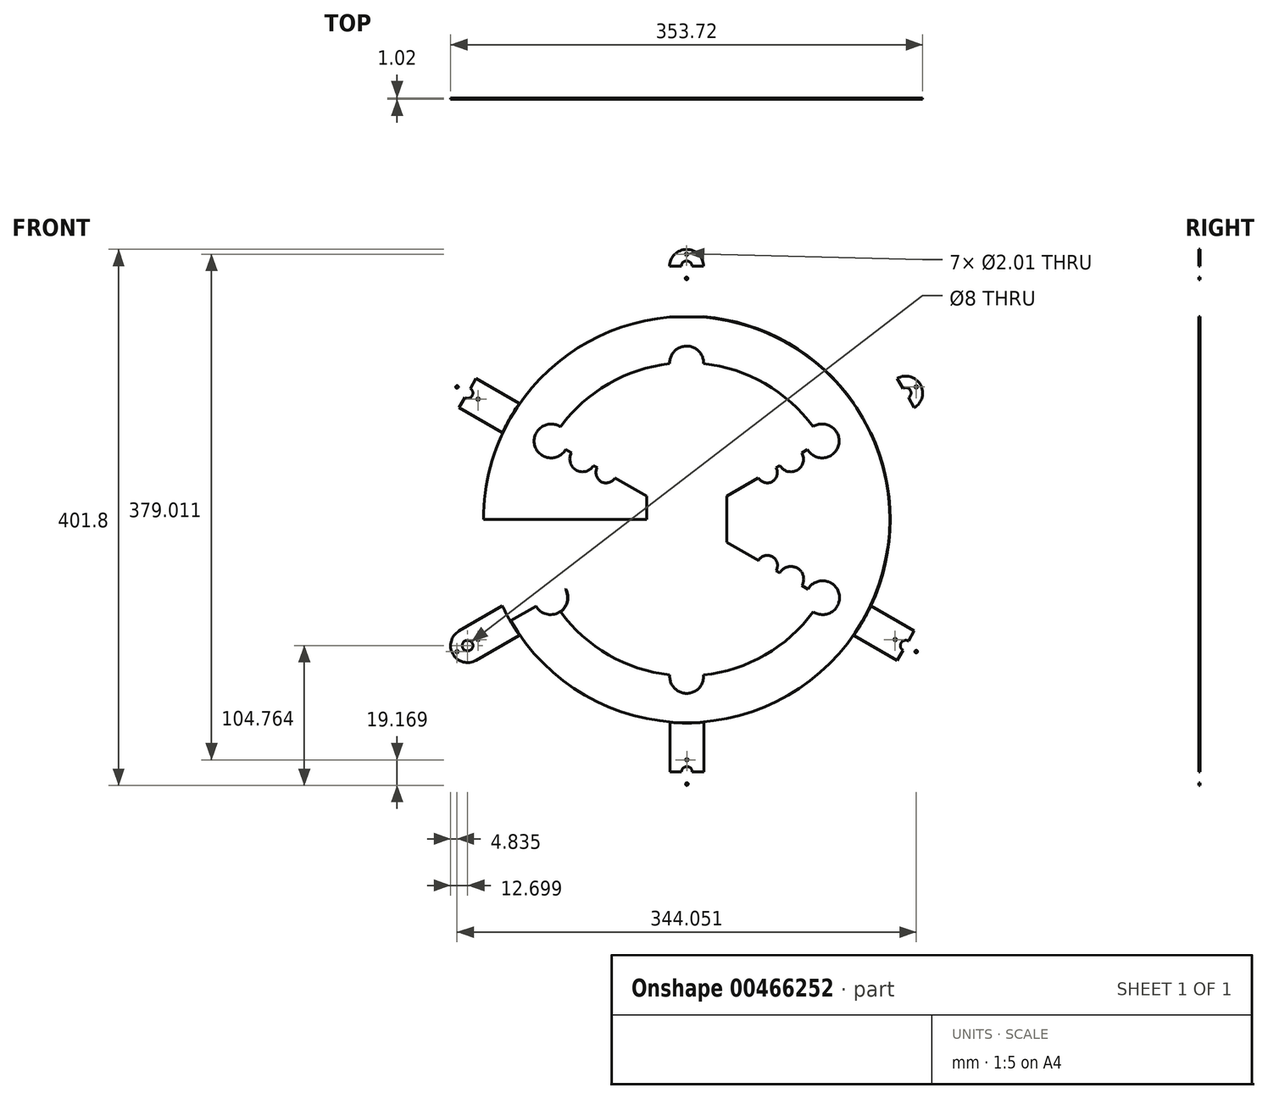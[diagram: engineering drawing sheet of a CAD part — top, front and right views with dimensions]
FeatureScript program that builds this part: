
annotation { "Feature Type Name" : "Feature", "Feature Type Description" : "" }
export const myFeature = defineFeature(function(context is Context, id is Id, definition is map)
    precondition{}
    {
        {
            var Q0;
            Q0=qCreatedBy(makeId("Front.planeOp"),FACE);
            var sketch = newSketch(context, id + "F0", { "sketchPlane" : qUnion([Q0])});
            skLineSegment(sketch, "E0.bottom", {"start": v(-43.08, 117.05) * mm, "end": v(16.87, 117.05) * mm});
            skLineSegment(sketch, "E0.top", {"start": v(-43.08, -42.97) * mm, "end": v(16.87, -42.97) * mm});
            skLineSegment(sketch, "E0.left", {"start": v(-43.08, 117.05) * mm, "end": v(-43.08, -42.97) * mm});
            skLineSegment(sketch, "E0.right", {"start": v(16.87, 117.05) * mm, "end": v(16.87, -42.97) * mm});
            skSolve(sketch);
        }
        {
            var Q0;
            Q0=makeQuery(id+"F0.imprint","IMPRINT",FACE,{"disambiguationData":[TD([[makeQuery(id+"F0.imprint","IMPRINT",EDGE,{"derivedFrom":sQuery(id+"F0.wireOp",EDGE,"E0.bottom")}),-1.0]])]});
            extrude(context, id + "F1", {"entities" : qUnion([Q0]), "depth" : 5.08 * mm});
        }
        {
            var Q0;
            Q0=makeQuery(id+"F1.opExtrude","SWEPT_BODY",BODY,{"disambiguationData":[OSD([sQuery(id+"F0.wireOp",EDGE,"E0.bottom"),sQuery(id+"F0.wireOp",EDGE,"E0.top"),sQuery(id+"F0.wireOp",EDGE,"E0.left"),sQuery(id+"F0.wireOp",EDGE,"E0.right")])]});
            deleteBodies(context, id + "F2", {"entities" : qUnion([Q0])});
        }
        {
            var Q0;
            Q0=qCreatedBy(makeId("Front.planeOp"),FACE);
            var sketch = newSketch(context, id + "F3", { "sketchPlane" : qUnion([Q0])});
            skCircle(sketch, "E1", {"center": v(0, 0) * mm, "radius": 152.4 * mm});
            skCircle(sketch, "E2", {"center": v(0, 117.47) * mm, "radius": 12.7 * mm});
            skCircle(sketch, "E3", {"center": v(0, -117.47) * mm, "radius": 12.7 * mm});
            skCircle(sketch, "E4", {"center": v(-101.56, 59.05) * mm, "radius": 12.7 * mm});
            skCircle(sketch, "E5", {"center": v(-101.91, -58.43) * mm, "radius": 12.7 * mm});
            skCircle(sketch, "E6.MirrorC", {"center": v(0.18, 0.3) * mm, "radius": 152.4 * mm});
            skLineSegment(sketch, "E7", {"start": v(0, 152.7) * mm, "end": v(0, -152.1) * mm});
            skLineSegment(sketch, "E8", {"start": v(-131.8, 76.5) * mm, "end": v(132.16, -75.9) * mm});
            skCircle(sketch, "E9.MirrorC", {"center": v(101.56, 59.05) * mm, "radius": 12.7 * mm});
            skLineSegment(sketch, "E10.MirrorCS", {"start": v(131.8, 76.5) * mm, "end": v(-132.16, -75.9) * mm});
            skCircle(sketch, "E11.MirrorC", {"center": v(101.91, -58.43) * mm, "radius": 12.7 * mm});
            skCircle(sketch, "E12", {"center": v(-78.02, 45.46) * mm, "radius": 9.53 * mm});
            skCircle(sketch, "E13", {"center": v(-60.31, 35.23) * mm, "radius": 7.62 * mm});
            skCircle(sketch, "E14", {"center": v(0.18, 0.3) * mm, "radius": 117.35 * mm});
            skLineSegment(sketch, "E15.bottom", {"start": v(29.97, 38.1) * mm, "end": v(-29.97, 38.1) * mm});
            skLineSegment(sketch, "E15.top", {"start": v(29.97, -38.1) * mm, "end": v(-29.97, -38.1) * mm});
            skLineSegment(sketch, "E15.left", {"start": v(29.97, 38.1) * mm, "end": v(29.97, -38.1) * mm});
            skLineSegment(sketch, "E15.right", {"start": v(-29.97, 38.1) * mm, "end": v(-29.97, -38.1) * mm});
            skCircle(sketch, "E16.MirrorC", {"center": v(78.02, 45.46) * mm, "radius": 9.53 * mm});
            skCircle(sketch, "E17.MirrorC", {"center": v(60.31, 35.23) * mm, "radius": 7.62 * mm});
            skCircle(sketch, "E18.MirrorC", {"center": v(0, -69.23) * mm, "radius": 7.62 * mm});
            skCircle(sketch, "E19.MirrorC", {"center": v(0, -89.68) * mm, "radius": 9.53 * mm});
            skLineSegment(sketch, "E20", {"start": v(0.18, 0.3) * mm, "end": v(-172, 0.3) * mm});
            skCircle(sketch, "E21.MirrorC", {"center": v(-101.56, -58.43) * mm, "radius": 12.7 * mm});
            skCircle(sketch, "E22.MirrorC", {"center": v(-78.02, -44.84) * mm, "radius": 9.53 * mm});
            skCircle(sketch, "E23.MirrorC", {"center": v(-60.31, -34.62) * mm, "radius": 7.62 * mm});
            skCircle(sketch, "E24.MirrorC", {"center": v(0.18, 70.16) * mm, "radius": 7.62 * mm});
            skCircle(sketch, "E25.MirrorC", {"center": v(0.18, 90.6) * mm, "radius": 9.53 * mm});
            skCircle(sketch, "E26.MirrorC", {"center": v(60.5, -34.3) * mm, "radius": 7.62 * mm});
            skCircle(sketch, "E27.MirrorC", {"center": v(78.2, -44.53) * mm, "radius": 9.53 * mm});
            skCircle(sketch, "E28.MirrorC", {"center": v(-0.18, 0.3) * mm, "radius": 152.4 * mm});
            skLineSegment(sketch, "E29.bottom", {"start": v(0, 151.87) * mm, "end": v(-12.7, 151.87) * mm});
            skLineSegment(sketch, "E29.top", {"start": v(0, 189.97) * mm, "end": v(-12.7, 189.97) * mm});
            skLineSegment(sketch, "E29.left", {"start": v(0, 151.87) * mm, "end": v(0, 189.97) * mm});
            skLineSegment(sketch, "E29.right", {"start": v(-12.7, 151.87) * mm, "end": v(-12.7, 189.97) * mm});
            skLineSegment(sketch, "E30.MirrorCS", {"start": v(12.7, 151.87) * mm, "end": v(12.7, 189.97) * mm});
            skLineSegment(sketch, "E31.MirrorCS", {"start": v(0, 189.97) * mm, "end": v(12.7, 189.97) * mm});
            skLineSegment(sketch, "E32.MirrorCS", {"start": v(0, 151.87) * mm, "end": v(12.7, 151.87) * mm});
            skArc(sketch, "E33", {"start": v(12.7, 189.97) * mm, "mid": v(0, 202.67) * mm, "end": v(-12.7, 189.97) * mm});
            skCircle(sketch, "E34", {"center": v(0, 189.97) * mm, "radius": 4 * mm});
            skCircle(sketch, "E35", {"center": v(0, 199.05) * mm, "radius": 1 * mm});
            skCircle(sketch, "E36", {"center": v(0, 180.89) * mm, "radius": 1 * mm});
            skCircle(sketch, "E37.MirrorC", {"center": v(172.03, -98.9) * mm, "radius": 1 * mm});
            skCircle(sketch, "E38.MirrorC", {"center": v(156.3, -89.83) * mm, "radius": 1 * mm});
            skLineSegment(sketch, "E39.MirrorCS", {"start": v(164.16, -94.37) * mm, "end": v(157.81, -105.36) * mm});
            skLineSegment(sketch, "E40.MirrorCS", {"start": v(164.16, -94.37) * mm, "end": v(170.51, -83.37) * mm});
            skCircle(sketch, "E41.MirrorC", {"center": v(164.16, -94.37) * mm, "radius": 4 * mm});
            skLineSegment(sketch, "E42.MirrorCS", {"start": v(131.17, -75.32) * mm, "end": v(164.16, -94.37) * mm});
            skArc(sketch, "E43.MirrorCS", {"start": v(170.51, -83.37) * mm, "mid": v(175.16, -100.72) * mm, "end": v(157.81, -105.36) * mm});
            skLineSegment(sketch, "E44.MirrorCS", {"start": v(124.82, -86.31) * mm, "end": v(157.81, -105.36) * mm});
            skLineSegment(sketch, "E45.MirrorCS", {"start": v(137.52, -64.32) * mm, "end": v(170.51, -83.37) * mm});
            skCircle(sketch, "E46.MirrorC", {"center": v(-156.3, -89.83) * mm, "radius": 1 * mm});
            skCircle(sketch, "E47.MirrorC", {"center": v(-172.03, -98.9) * mm, "radius": 1 * mm});
            skLineSegment(sketch, "E48.MirrorCS", {"start": v(-131.17, -75.32) * mm, "end": v(-164.16, -94.37) * mm});
            skLineSegment(sketch, "E49.MirrorCS", {"start": v(-137.52, -64.32) * mm, "end": v(-170.51, -83.37) * mm});
            skLineSegment(sketch, "E50.MirrorCS", {"start": v(-164.16, -94.37) * mm, "end": v(-157.81, -105.36) * mm});
            skArc(sketch, "E51.MirrorCS", {"start": v(-170.51, -83.37) * mm, "mid": v(-175.16, -100.72) * mm, "end": v(-157.81, -105.36) * mm});
            skLineSegment(sketch, "E52.MirrorCS", {"start": v(-124.82, -86.31) * mm, "end": v(-157.81, -105.36) * mm});
            skCircle(sketch, "E53.MirrorC", {"center": v(-164.16, -94.37) * mm, "radius": 4 * mm});
            skLineSegment(sketch, "E54.MirrorCS", {"start": v(-164.16, -94.37) * mm, "end": v(-170.51, -83.37) * mm});
            skCircle(sketch, "E55.MirrorC", {"center": v(-164.16, 94.99) * mm, "radius": 4 * mm});
            skLineSegment(sketch, "E56.MirrorCS", {"start": v(-137.52, 64.94) * mm, "end": v(-170.51, 83.99) * mm});
            skLineSegment(sketch, "E57.MirrorCS", {"start": v(-164.16, 94.99) * mm, "end": v(-157.81, 105.98) * mm});
            skLineSegment(sketch, "E58.MirrorCS", {"start": v(-164.16, 94.99) * mm, "end": v(-170.51, 83.99) * mm});
            skCircle(sketch, "E59.MirrorC", {"center": v(-156.3, 90.45) * mm, "radius": 1 * mm});
            skCircle(sketch, "E60.MirrorC", {"center": v(-172.03, 99.53) * mm, "radius": 1 * mm});
            skLineSegment(sketch, "E61.MirrorCS", {"start": v(-131.17, 75.94) * mm, "end": v(-164.16, 94.99) * mm});
            skArc(sketch, "E62.MirrorCS", {"start": v(-170.51, 83.99) * mm, "mid": v(-175.16, 101.34) * mm, "end": v(-157.81, 105.98) * mm});
            skLineSegment(sketch, "E63.MirrorCS", {"start": v(-124.82, 86.93) * mm, "end": v(-157.81, 105.98) * mm});
            skCircle(sketch, "E64.MirrorC", {"center": v(164.16, 94.99) * mm, "radius": 4 * mm});
            skLineSegment(sketch, "E65.MirrorCS", {"start": v(164.16, 94.99) * mm, "end": v(170.51, 83.99) * mm});
            skLineSegment(sketch, "E66.MirrorCS", {"start": v(164.16, 94.99) * mm, "end": v(157.81, 105.98) * mm});
            skLineSegment(sketch, "E67.MirrorCS", {"start": v(124.82, 86.93) * mm, "end": v(157.81, 105.98) * mm});
            skLineSegment(sketch, "E68.MirrorCS", {"start": v(131.17, 75.94) * mm, "end": v(164.16, 94.99) * mm});
            skCircle(sketch, "E69.MirrorC", {"center": v(156.3, 90.45) * mm, "radius": 1 * mm});
            skCircle(sketch, "E70.MirrorC", {"center": v(172.03, 99.53) * mm, "radius": 1 * mm});
            skLineSegment(sketch, "E71.MirrorCS", {"start": v(137.52, 64.94) * mm, "end": v(170.51, 83.99) * mm});
            skArc(sketch, "E72.MirrorCS", {"start": v(170.51, 83.99) * mm, "mid": v(175.16, 101.34) * mm, "end": v(157.81, 105.98) * mm});
            skCircle(sketch, "E73.MirrorC", {"center": v(0.18, -189.04) * mm, "radius": 4 * mm});
            skLineSegment(sketch, "E74.MirrorCS", {"start": v(-12.52, -150.94) * mm, "end": v(-12.52, -189.04) * mm});
            skLineSegment(sketch, "E75.MirrorCS", {"start": v(0.18, -189.04) * mm, "end": v(-12.52, -189.04) * mm});
            skLineSegment(sketch, "E76.MirrorCS", {"start": v(0.18, -189.04) * mm, "end": v(12.88, -189.04) * mm});
            skCircle(sketch, "E77.MirrorC", {"center": v(0.18, -179.96) * mm, "radius": 1 * mm});
            skLineSegment(sketch, "E78.MirrorCS", {"start": v(0.18, -150.94) * mm, "end": v(0.18, -189.04) * mm});
            skCircle(sketch, "E79.MirrorC", {"center": v(0.18, -198.12) * mm, "radius": 1 * mm});
            skLineSegment(sketch, "E80.MirrorCS", {"start": v(12.88, -150.94) * mm, "end": v(12.88, -189.04) * mm});
            skArc(sketch, "E81.MirrorCS", {"start": v(12.88, -189.04) * mm, "mid": v(0.18, -201.74) * mm, "end": v(-12.52, -189.04) * mm});
            skSolve(sketch);
        }
        {
            var Q0;
            {var subQ4=sQuery(id+"F3.wireOp",EDGE,"E1");var subQ5=makeQuery(id+"F3.imprint","INTERSECT",VERTEX,{"derivedFrom":[subQ4,sQuery(id+"F3.wireOp",EDGE,"E61.MirrorCS")]});Q0=makeQuery(id+"F3.imprint","IMPRINT",FACE,{"disambiguationData":[TD([[makeQuery(id+"F3.imprint","IMPRINT",EDGE,{"disambiguationData":[TD([[subQ5,1.0]])],"derivedFrom":subQ4}),1.0]])]});}
            var Q1;
            {var subQ3=sQuery(id+"F3.wireOp",EDGE,"E5");var subQ10=sQuery(id+"F3.wireOp",EDGE,"E14");var subQ11=makeQuery(id+"F3.imprint","INTERSECT",VERTEX,{"disambiguationData":[OD(0.0)],"derivedFrom":[subQ3,subQ10]});Q1=makeQuery(id+"F3.imprint","IMPRINT",FACE,{"disambiguationData":[TD([[makeQuery(id+"F3.imprint","IMPRINT",EDGE,{"disambiguationData":[TD([[subQ11,-1.0]])],"derivedFrom":subQ3}),-1.0]])]});}
            var Q2;
            {var subQ3=sQuery(id+"F3.wireOp",EDGE,"E21.MirrorC");var subQ13=sQuery(id+"F3.wireOp",EDGE,"E5");var subQ14=makeQuery(id+"F3.imprint","INTERSECT",VERTEX,{"disambiguationData":[OD(0.0)],"derivedFrom":[subQ13,subQ3]});Q2=makeQuery(id+"F3.imprint","IMPRINT",FACE,{"disambiguationData":[TD([[makeQuery(id+"F3.imprint","IMPRINT",EDGE,{"disambiguationData":[TD([[subQ14,-1.0]])],"derivedFrom":subQ13}),-1.0]])]});}
            var Q3;
            {var subQ11=sQuery(id+"F3.wireOp",EDGE,"E4");var subQ13=sQuery(id+"F3.wireOp",EDGE,"E14");var subQ14=makeQuery(id+"F3.imprint","INTERSECT",VERTEX,{"disambiguationData":[OD(1.0)],"derivedFrom":[subQ11,subQ13]});Q3=makeQuery(id+"F3.imprint","IMPRINT",FACE,{"disambiguationData":[TD([[makeQuery(id+"F3.imprint","IMPRINT",EDGE,{"disambiguationData":[TD([[subQ14,-1.0]])],"derivedFrom":subQ11}),-1.0]])]});}
            var Q4;
            {var subQ10=sQuery(id+"F3.wireOp",EDGE,"E3");var subQ12=sQuery(id+"F3.wireOp",EDGE,"E14");var subQ13=makeQuery(id+"F3.imprint","INTERSECT",VERTEX,{"disambiguationData":[OD(1.0)],"derivedFrom":[subQ10,subQ12]});Q4=makeQuery(id+"F3.imprint","IMPRINT",FACE,{"disambiguationData":[TD([[makeQuery(id+"F3.imprint","IMPRINT",EDGE,{"disambiguationData":[TD([[subQ13,-1.0]])],"derivedFrom":subQ10}),-1.0]])]});}
            var Q5;
            {var subQ8=sQuery(id+"F3.wireOp",EDGE,"E7");var subQ11=sQuery(id+"F3.wireOp",EDGE,"E3");var subQ18=makeQuery(id+"F3.imprint","INTERSECT",VERTEX,{"disambiguationData":[OD(0.0)],"derivedFrom":[subQ11,subQ8]});Q5=makeQuery(id+"F3.imprint","IMPRINT",FACE,{"disambiguationData":[TD([[makeQuery(id+"F3.imprint","IMPRINT",EDGE,{"disambiguationData":[TD([[subQ18,-1.0]])],"derivedFrom":subQ11}),-1.0]])]});}
            var Q6;
            {var subQ3=sQuery(id+"F3.wireOp",EDGE,"E7");var subQ9=sQuery(id+"F3.wireOp",EDGE,"E3");var subQ10=makeQuery(id+"F3.imprint","INTERSECT",VERTEX,{"disambiguationData":[OD(0.0)],"derivedFrom":[subQ9,subQ3]});Q6=makeQuery(id+"F3.imprint","IMPRINT",FACE,{"disambiguationData":[TD([[makeQuery(id+"F3.imprint","IMPRINT",EDGE,{"disambiguationData":[TD([[subQ10,1.0]])],"derivedFrom":subQ9}),-1.0]])]});}
            var Q7;
            {var subQ3=sQuery(id+"F3.wireOp",EDGE,"E14");var subQ11=sQuery(id+"F3.wireOp",EDGE,"E3");var subQ13=makeQuery(id+"F3.imprint","INTERSECT",VERTEX,{"disambiguationData":[OD(0.0)],"derivedFrom":[subQ11,subQ3]});Q7=makeQuery(id+"F3.imprint","IMPRINT",FACE,{"disambiguationData":[TD([[makeQuery(id+"F3.imprint","IMPRINT",EDGE,{"disambiguationData":[TD([[subQ13,1.0]])],"derivedFrom":subQ11}),-1.0]])]});}
            var Q8;
            {var subQ4=sQuery(id+"F3.wireOp",EDGE,"E80.MirrorCS");var subQ10=sQuery(id+"F3.wireOp",EDGE,"E1");var subQ11=makeQuery(id+"F3.imprint","INTERSECT",VERTEX,{"derivedFrom":[subQ10,subQ4]});Q8=makeQuery(id+"F3.imprint","IMPRINT",FACE,{"disambiguationData":[TD([[makeQuery(id+"F3.imprint","IMPRINT",EDGE,{"disambiguationData":[TD([[subQ11,1.0]])],"derivedFrom":subQ10}),-1.0]])]});}
            var Q9;
            {var subQ1=sQuery(id+"F3.wireOp",EDGE,"E74.MirrorCS");var subQ3=sQuery(id+"F3.wireOp",EDGE,"E1");var subQ4=makeQuery(id+"F3.imprint","INTERSECT",VERTEX,{"derivedFrom":[subQ3,subQ1]});Q9=makeQuery(id+"F3.imprint","IMPRINT",FACE,{"disambiguationData":[TD([[makeQuery(id+"F3.imprint","IMPRINT",EDGE,{"disambiguationData":[TD([[subQ4,-1.0]])],"derivedFrom":subQ3}),-1.0]])]});}
            var Q10;
            Q10=makeQuery(id+"F3.imprint","IMPRINT",FACE,{"disambiguationData":[TD([[makeQuery(id+"F3.imprint","IMPRINT",EDGE,{"derivedFrom":sQuery(id+"F3.wireOp",EDGE,"E79.MirrorC")}),1.0]])]});
            var Q11;
            {var subQ1=sQuery(id+"F3.wireOp",EDGE,"E1");var subQ5=sQuery(id+"F3.wireOp",EDGE,"E52.MirrorCS");var subQ10=makeQuery(id+"F3.imprint","INTERSECT",VERTEX,{"derivedFrom":[subQ1,subQ5]});Q11=makeQuery(id+"F3.imprint","IMPRINT",FACE,{"disambiguationData":[TD([[makeQuery(id+"F3.imprint","IMPRINT",EDGE,{"disambiguationData":[TD([[subQ10,1.0]])],"derivedFrom":subQ1}),-1.0]])]});}
            var Q12;
            {var subQ4=sQuery(id+"F3.wireOp",EDGE,"E1");var subQ11=sQuery(id+"F3.wireOp",EDGE,"E28.MirrorC");var subQ13=makeQuery(id+"F3.imprint","INTERSECT",VERTEX,{"disambiguationData":[OD(1.0)],"derivedFrom":[subQ4,subQ11]});Q12=makeQuery(id+"F3.imprint","IMPRINT",FACE,{"disambiguationData":[TD([[makeQuery(id+"F3.imprint","IMPRINT",EDGE,{"disambiguationData":[TD([[subQ13,-1.0]])],"derivedFrom":subQ4}),-1.0]])]});}
            var Q13;
            Q13=makeQuery(id+"F3.imprint","IMPRINT",FACE,{"disambiguationData":[TD([[makeQuery(id+"F3.imprint","IMPRINT",EDGE,{"derivedFrom":sQuery(id+"F3.wireOp",EDGE,"E47.MirrorC")}),-1.0]])]});
            var Q14;
            {var subQ3=sQuery(id+"F3.wireOp",EDGE,"E1");var subQ16=makeQuery(id+"F3.imprint","INTERSECT",VERTEX,{"derivedFrom":[subQ3,sQuery(id+"F3.wireOp",EDGE,"E68.MirrorCS")]});Q14=makeQuery(id+"F3.imprint","IMPRINT",FACE,{"disambiguationData":[TD([[makeQuery(id+"F3.imprint","IMPRINT",EDGE,{"disambiguationData":[TD([[subQ16,1.0]])],"derivedFrom":subQ3}),1.0]])]});}
            var Q15;
            {var subQ5=sQuery(id+"F3.wireOp",EDGE,"E42.MirrorCS");var subQ6=sQuery(id+"F3.wireOp",EDGE,"E1");var subQ7=makeQuery(id+"F3.imprint","INTERSECT",VERTEX,{"derivedFrom":[subQ6,subQ5]});Q15=makeQuery(id+"F3.imprint","IMPRINT",FACE,{"disambiguationData":[TD([[makeQuery(id+"F3.imprint","IMPRINT",EDGE,{"disambiguationData":[TD([[subQ7,-1.0]])],"derivedFrom":subQ6}),-1.0]])]});}
            var Q16;
            {var subQ8=sQuery(id+"F3.wireOp",EDGE,"E44.MirrorCS");var subQ10=sQuery(id+"F3.wireOp",EDGE,"E1");var subQ11=makeQuery(id+"F3.imprint","INTERSECT",VERTEX,{"derivedFrom":[subQ10,subQ8]});Q16=makeQuery(id+"F3.imprint","IMPRINT",FACE,{"disambiguationData":[TD([[makeQuery(id+"F3.imprint","IMPRINT",EDGE,{"disambiguationData":[TD([[subQ11,-1.0]])],"derivedFrom":subQ10}),-1.0]])]});}
            var Q17;
            Q17=makeQuery(id+"F3.imprint","IMPRINT",FACE,{"disambiguationData":[TD([[makeQuery(id+"F3.imprint","IMPRINT",EDGE,{"derivedFrom":sQuery(id+"F3.wireOp",EDGE,"E37.MirrorC")}),1.0]])]});
            var Q18;
            {var subQ1=sQuery(id+"F3.wireOp",EDGE,"E8");var subQ8=sQuery(id+"F3.wireOp",EDGE,"E15.left");var subQ17=makeQuery(id+"F3.imprint","INTERSECT",VERTEX,{"derivedFrom":[subQ1,subQ8]});Q18=makeQuery(id+"F3.imprint","IMPRINT",FACE,{"disambiguationData":[TD([[makeQuery(id+"F3.imprint","IMPRINT",EDGE,{"disambiguationData":[TD([[subQ17,-1.0]])],"derivedFrom":subQ1}),1.0]])]});}
            var Q19;
            {var subQ0=sQuery(id+"F3.wireOp",EDGE,"E71.MirrorCS");var subQ6=sQuery(id+"F3.wireOp",EDGE,"E6.MirrorC");var subQ11=makeQuery(id+"F3.imprint","INTERSECT",VERTEX,{"derivedFrom":[subQ6,subQ0]});Q19=makeQuery(id+"F3.imprint","IMPRINT",FACE,{"disambiguationData":[TD([[makeQuery(id+"F3.imprint","IMPRINT",EDGE,{"disambiguationData":[TD([[subQ11,1.0]])],"derivedFrom":subQ6}),1.0]])]});}
            var Q20;
            {var subQ0=sQuery(id+"F3.wireOp",EDGE,"E67.MirrorCS");var subQ7=sQuery(id+"F3.wireOp",EDGE,"E6.MirrorC");var subQ11=makeQuery(id+"F3.imprint","INTERSECT",VERTEX,{"derivedFrom":[subQ7,subQ0]});Q20=makeQuery(id+"F3.imprint","IMPRINT",FACE,{"disambiguationData":[TD([[makeQuery(id+"F3.imprint","IMPRINT",EDGE,{"disambiguationData":[TD([[subQ11,-1.0]])],"derivedFrom":subQ7}),1.0]])]});}
            var Q21;
            Q21=makeQuery(id+"F3.imprint","IMPRINT",FACE,{"disambiguationData":[TD([[makeQuery(id+"F3.imprint","IMPRINT",EDGE,{"derivedFrom":sQuery(id+"F3.wireOp",EDGE,"E70.MirrorC")}),-1.0]])]});
            var Q22;
            {var subQ0=sQuery(id+"F3.wireOp",EDGE,"E32.MirrorCS");Q22=makeQuery(id+"F3.imprint","IMPRINT",FACE,{"disambiguationData":[TD([[makeQuery(id+"F3.imprint","IMPRINT",EDGE,{"derivedFrom":subQ0}),-1.0]])]});}
            var Q23;
            {var subQ3=sQuery(id+"F3.wireOp",EDGE,"E7");var subQ6=sQuery(id+"F3.wireOp",EDGE,"E2");var subQ15=makeQuery(id+"F3.imprint","INTERSECT",VERTEX,{"disambiguationData":[OD(1.0)],"derivedFrom":[subQ6,subQ3]});Q23=makeQuery(id+"F3.imprint","IMPRINT",FACE,{"disambiguationData":[TD([[makeQuery(id+"F3.imprint","IMPRINT",EDGE,{"disambiguationData":[TD([[subQ15,-1.0]])],"derivedFrom":subQ6}),-1.0]])]});}
            var Q24;
            {var subQ5=sQuery(id+"F3.wireOp",EDGE,"E2");var subQ20=sQuery(id+"F3.wireOp",EDGE,"E14");var subQ21=makeQuery(id+"F3.imprint","INTERSECT",VERTEX,{"disambiguationData":[OD(0.0)],"derivedFrom":[subQ5,subQ20]});Q24=makeQuery(id+"F3.imprint","IMPRINT",FACE,{"disambiguationData":[TD([[makeQuery(id+"F3.imprint","IMPRINT",EDGE,{"disambiguationData":[TD([[subQ21,-1.0]])],"derivedFrom":subQ5}),-1.0]])]});}
            var Q25;
            {var subQ5=sQuery(id+"F3.wireOp",EDGE,"E29.left");var subQ9=sQuery(id+"F3.wireOp",EDGE,"E36");var subQ11=makeQuery(id+"F3.imprint","INTERSECT",VERTEX,{"disambiguationData":[OD(1.0)],"derivedFrom":[subQ5,subQ9]});Q25=makeQuery(id+"F3.imprint","IMPRINT",FACE,{"disambiguationData":[TD([[makeQuery(id+"F3.imprint","IMPRINT",EDGE,{"disambiguationData":[TD([[subQ11,-1.0]])],"derivedFrom":subQ5}),1.0]])]});}
            var Q26;
            {var subQ5=sQuery(id+"F3.wireOp",EDGE,"E36");var subQ6=sQuery(id+"F3.wireOp",EDGE,"E29.left");var subQ7=makeQuery(id+"F3.imprint","INTERSECT",VERTEX,{"disambiguationData":[OD(1.0)],"derivedFrom":[subQ6,subQ5]});Q26=makeQuery(id+"F3.imprint","IMPRINT",FACE,{"disambiguationData":[TD([[makeQuery(id+"F3.imprint","IMPRINT",EDGE,{"disambiguationData":[TD([[subQ7,-1.0]])],"derivedFrom":subQ6}),-1.0]])]});}
            var Q27;
            {var subQ5=sQuery(id+"F3.wireOp",EDGE,"E33");Q27=makeQuery(id+"F3.imprint","IMPRINT",FACE,{"disambiguationData":[TD([[makeQuery(id+"F3.imprint","IMPRINT",EDGE,{"derivedFrom":subQ5}),1.0]])]});}
            var Q28;
            {var subQ1=sQuery(id+"F3.wireOp",EDGE,"E56.MirrorCS");var subQ5=sQuery(id+"F3.wireOp",EDGE,"E28.MirrorC");var subQ6=makeQuery(id+"F3.imprint","INTERSECT",VERTEX,{"derivedFrom":[subQ5,subQ1]});Q28=makeQuery(id+"F3.imprint","IMPRINT",FACE,{"disambiguationData":[TD([[makeQuery(id+"F3.imprint","IMPRINT",EDGE,{"disambiguationData":[TD([[subQ6,1.0]])],"derivedFrom":subQ5}),-1.0]])]});}
            var Q29;
            {var subQ8=sQuery(id+"F3.wireOp",EDGE,"E63.MirrorCS");var subQ10=sQuery(id+"F3.wireOp",EDGE,"E28.MirrorC");var subQ11=makeQuery(id+"F3.imprint","INTERSECT",VERTEX,{"derivedFrom":[subQ10,subQ8]});Q29=makeQuery(id+"F3.imprint","IMPRINT",FACE,{"disambiguationData":[TD([[makeQuery(id+"F3.imprint","IMPRINT",EDGE,{"disambiguationData":[TD([[subQ11,-1.0]])],"derivedFrom":subQ10}),-1.0]])]});}
            var Q30;
            Q30=makeQuery(id+"F3.imprint","IMPRINT",FACE,{"disambiguationData":[TD([[makeQuery(id+"F3.imprint","IMPRINT",EDGE,{"derivedFrom":sQuery(id+"F3.wireOp",EDGE,"E60.MirrorC")}),1.0]])]});
            var Q31;
            {var subQ9=sQuery(id+"F3.wireOp",EDGE,"E29.bottom");Q31=makeQuery(id+"F3.imprint","IMPRINT",FACE,{"disambiguationData":[TD([[makeQuery(id+"F3.imprint","IMPRINT",EDGE,{"derivedFrom":subQ9}),1.0]])]});}
            extrude(context, id + "F4", {"entities" : qUnion([Q0, Q1, Q2, Q3, Q4, Q5, Q6, Q7, Q8, Q9, Q10, Q11, Q12, Q13, Q14, Q15, Q16, Q17, Q18, Q19, Q20, Q21, Q22, Q23, Q24, Q25, Q26, Q27, Q28, Q29, Q30, Q31]), "depth" : 1.02 * mm});
        }
    });
